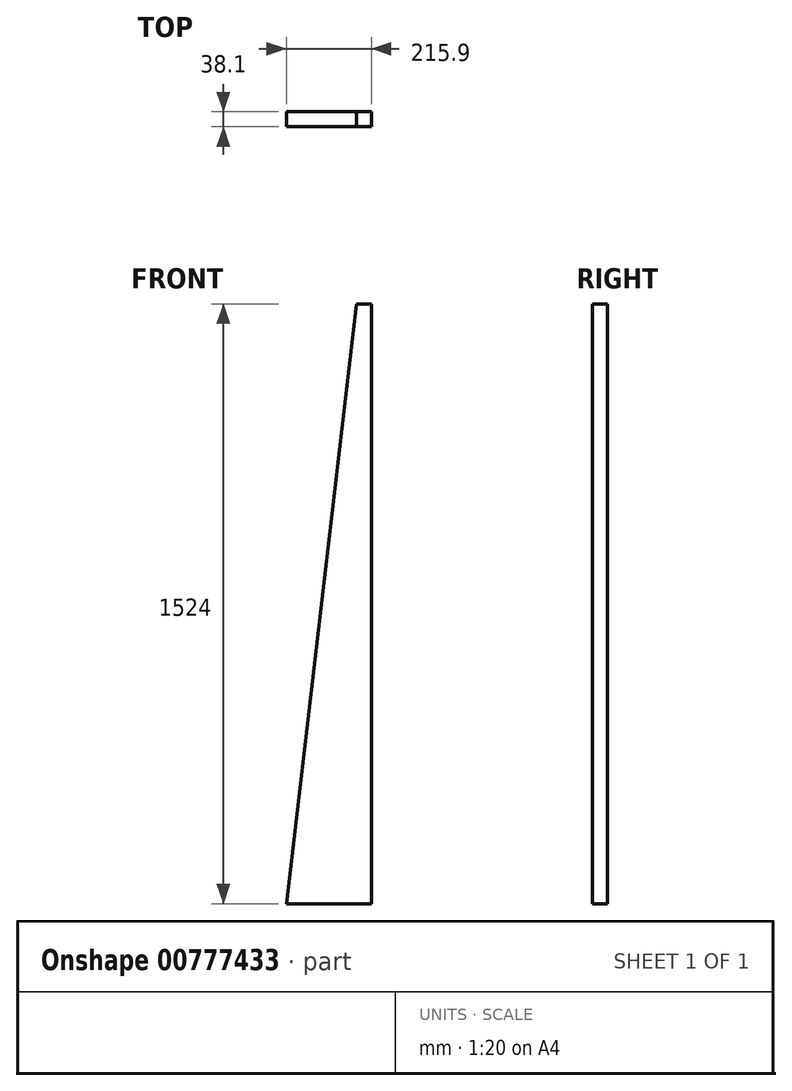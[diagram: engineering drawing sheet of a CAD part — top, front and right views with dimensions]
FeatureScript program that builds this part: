
annotation { "Feature Type Name" : "Feature", "Feature Type Description" : "" }
export const myFeature = defineFeature(function(context is Context, id is Id, definition is map)
    precondition{}
    {
        {
            var Q0;
            Q0=qCreatedBy(makeId("Front.planeOp"),FACE);
            var sketch = newSketch(context, id + "F0", { "sketchPlane" : qUnion([Q0])});
            skLineSegment(sketch, "E0", {"start": v(0, 0) * mm, "end": v(215.9, 0) * mm});
            skLineSegment(sketch, "E1", {"start": v(215.9, 0) * mm, "end": v(215.9, 1524) * mm});
            skLineSegment(sketch, "E2", {"start": v(215.9, 1524) * mm, "end": v(177.8, 1524) * mm});
            skLineSegment(sketch, "E3", {"start": v(177.8, 1524) * mm, "end": v(0, 0) * mm});
            skSolve(sketch);
        }
        {
            var Q0;
            Q0=makeQuery(id+"F0.imprint","IMPRINT",FACE,{"disambiguationData":[TD([[makeQuery(id+"F0.imprint","IMPRINT",EDGE,{"derivedFrom":sQuery(id+"F0.wireOp",EDGE,"E0")}),1.0]])]});
            extrude(context, id + "F1", {"entities" : qUnion([Q0]), "depth" : 38.1 * mm, "offsetDistance" : 25.4 * mm});
        }
    });
